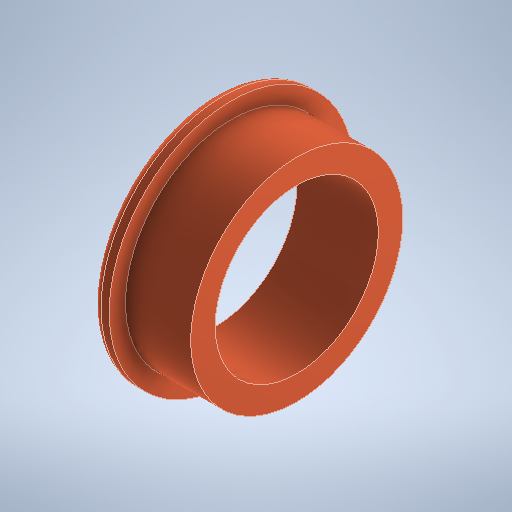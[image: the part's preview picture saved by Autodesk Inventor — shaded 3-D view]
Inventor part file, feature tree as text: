
AUTODESK INVENTOR PART (.ipt)
format: ipt  version: 2025.1 (Build 291241000, 241)  size: 283,136 bytes
history: native  units: mm
features: sketch x2, revolve x1, fillet x1, hole x1
ambient origin geometry x8: Origin, YZ Plane, XZ Plane, XY Plane, X Axis, Y Axis, Z Axis, Center Point
bodies: Solid1 (feature_tree)
feature tree (5):
  revolve  "Revolution1"  [1 undecoded]
  fillet  "Fillet1"  Radius=30.0mm
  hole  "Hole1"  [1 undecoded]
  sketch  "Sketch1"  dims[d0=2.0mm d1=8.0mm d2=30.0mm]
  sketch  "Sketch2"  dims[d3=26.0mm d4=90.0deg d5=1.0mm d6=20.0mm d7=6.0mm d8=4.0mm d9=2.0mm d10=90.0deg d11=8.0mm d12=0.0mm]
note: 2 required parameter values undecoded (feature->parameter linkage not recoverable at this tier; creation-order binding heuristic only, values carry confidence <= 0.55)